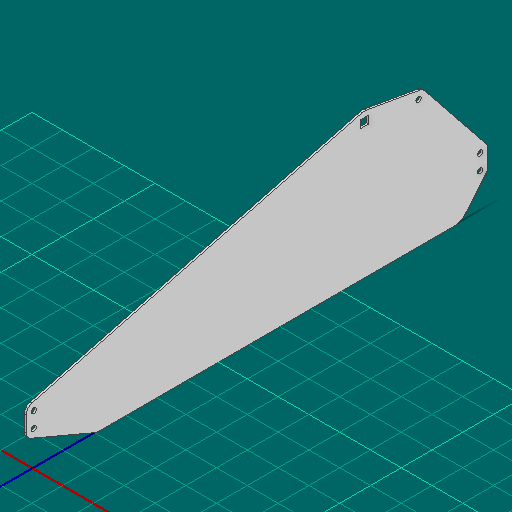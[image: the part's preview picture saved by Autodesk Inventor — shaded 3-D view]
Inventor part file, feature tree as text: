
AUTODESK INVENTOR PART (.ipt)
format: ipt  version: 2025 (Build 290162000, 162)  size: 144,384 bytes
history: native  units: in
note: dims shown in document units (in); Inventor stores cm internally (conversion verified against a paired STEP export)
features: other x4, extrude x1, sketch x1
ambient origin geometry x8: Origin, YZ Plane, XZ Plane, XY Plane, X Axis, Y Axis, Z Axis, Center Point
bodies: Solid1 (feature_tree)
feature tree (6):
  other  "Blocks"
  extrude  "Extrusion1"  Depth=0.5in
  sketch  "Sketch1"  dims[d0=0.5in d1=0.5in d2=1.0in d3=0.0625in d4=0.0in d6=0.5in d7=1.0in d8=0.2485in d9=0.2485in d10=0.625in]
  other  "maiin"
  other  "main"
  other  "main:1"
